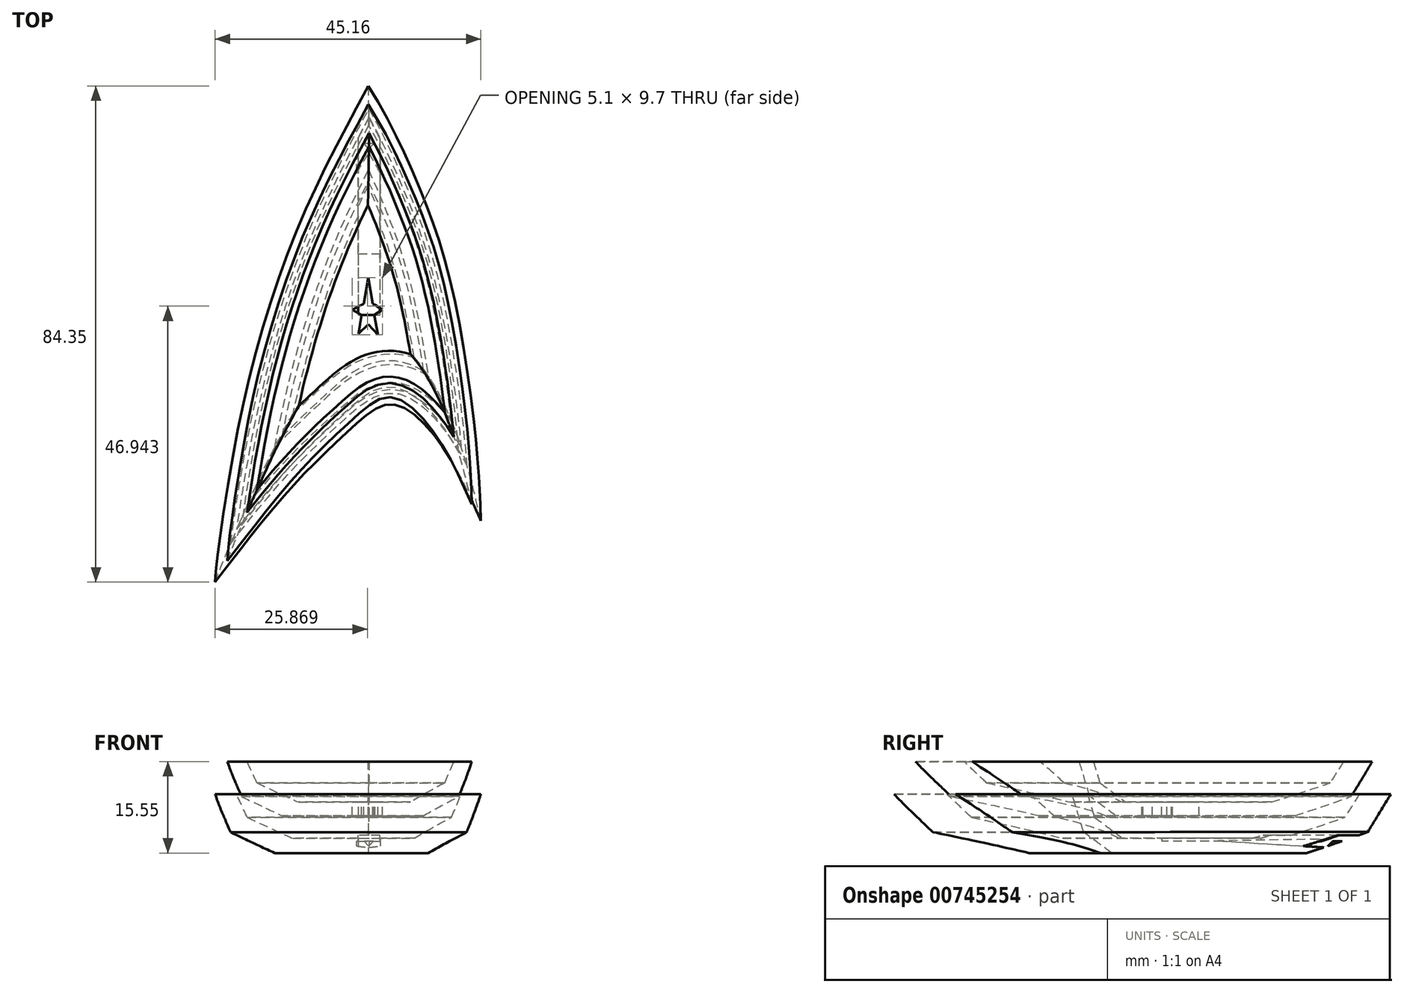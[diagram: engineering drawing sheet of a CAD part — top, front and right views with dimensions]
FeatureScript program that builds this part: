
annotation { "Feature Type Name" : "Feature", "Feature Type Description" : "" }
export const myFeature = defineFeature(function(context is Context, id is Id, definition is map)
    precondition{}
    {
        {
            var Q0;
            Q0=qCreatedBy(makeId("Top.planeOp"),FACE);
            var sketch = newSketch(context, id + "F0", { "sketchPlane" : qUnion([Q0])});
            skFitSpline(sketch, "E0", {"points": [v(0, 38.9) * mm, v(-11.48, 15.96) * mm, v(-21.55, -16.52) * mm, v(-25.85, -43.01) * mm, v(-26.03, -45.44) * mm], "startDerivative": vector(-41.53, -76.48) * mm, "endDerivative": vector(-0.94, -19.8) * mm});
            skFitSpline(sketch, "E1", {"points": [v(-26.03, -45.44) * mm, v(-12.6, -28.83) * mm, v(-2.7, -19.13) * mm, v(4.2, -15.2) * mm, v(12.4, -22.11) * mm, v(19.13, -34.99) * mm], "startDerivative": vector(53.97, 70.22) * mm, "endDerivative": vector(28.13, -63.45) * mm});
            skFitSpline(sketch, "E2", {"points": [v(0, 38.9) * mm, v(8.31, 22.5) * mm, v(14.28, 4.39) * mm, v(18.38, -22.3) * mm, v(19.13, -34.99) * mm], "startDerivative": vector(40.07, -63.37) * mm, "endDerivative": vector(1.63, -55.12) * mm});
            skSolve(sketch);
        }
        {
            var Q0;
            Q0=qCreatedBy(makeId("Top.planeOp"),FACE);
            cPlane(context, id + "F1", {"entities" : qUnion([Q0]), "cplaneType" : CPlaneType.OFFSET, "offset" : 25 * mm, "width" : 150 * mm, "height" : 150 * mm});
        }
        {
            var Q0;
            Q0=makeQuery(id+"F0.imprint","IMPRINT",FACE,{"disambiguationData":[TD([[makeQuery(id+"F0.imprint","IMPRINT",EDGE,{"derivedFrom":sQuery(id+"F0.wireOp",EDGE,"E0")}),1.0]])]});
            extrude(context, id + "F2", {"entities" : qUnion([Q0]), "depth" : 10 * mm, "offsetDistance" : 25 * mm});
        }
        {
            var Q0;
            Q0=makeQuery(id+"F2.opExtrude","CAP_EDGE",EDGE,{"disambiguationData":[OSD([sQuery(id+"F0.wireOp",EDGE,"E2")])],"isStart":true});
            var Q1;
            Q1=makeQuery(id+"F2.opExtrude","CAP_EDGE",EDGE,{"disambiguationData":[OSD([sQuery(id+"F0.wireOp",EDGE,"E1")])],"isStart":true});
            var Q2;
            Q2=makeQuery(id+"F2.opExtrude","CAP_EDGE",EDGE,{"disambiguationData":[OSD([sQuery(id+"F0.wireOp",EDGE,"E0")])],"isStart":true});
            chamfer(context, id + "F3", {"entities" : qUnion([Q0, Q1, Q2]), "chamferType" : ChamferType.TWO_OFFSETS, "width1" : 3 * mm, "oppositeDirection" : false, "width2" : 10 * mm, "tangentPropagation" : true});
        }
        {
            var Q0;
            Q0=makeQuery(id+"F2.opExtrude","CAP_FACE",FACE,{"disambiguationData":[OSD([sQuery(id+"F0.wireOp",EDGE,"E0"),sQuery(id+"F0.wireOp",EDGE,"E1"),sQuery(id+"F0.wireOp",EDGE,"E2")])],"isStart":false});
            shell(context, id + "F4", {"entities" : qUnion([Q0]), "thickness" : 2.5 * mm});
        }
        {
            var Q0;
            {var subQ0=sQuery(id+"F0.wireOp",EDGE,"E2");Q0=makeQuery(id+"F3.opChamfer","BLEND_EDGE",EDGE,{"blendedFrom":[makeQuery(id+"F2.opExtrude","CAP_EDGE",EDGE,{"disambiguationData":[OSD([subQ0])],"isStart":true}),makeQuery(id+"F2.opExtrude","CAP_FACE",FACE,{"disambiguationData":[OSD([sQuery(id+"F0.wireOp",EDGE,"E0"),sQuery(id+"F0.wireOp",EDGE,"E1"),subQ0])],"isStart":true})],"blendedInto":[makeQuery(id+"F2.opExtrude","CAP_FACE",FACE,{"disambiguationData":[OSD([sQuery(id+"F0.wireOp",EDGE,"E0"),sQuery(id+"F0.wireOp",EDGE,"E1"),subQ0])],"isStart":true})]});}
            var Q1;
            {var subQ0=sQuery(id+"F0.wireOp",EDGE,"E1");Q1=makeQuery(id+"F3.opChamfer","BLEND_EDGE",EDGE,{"blendedFrom":[makeQuery(id+"F2.opExtrude","CAP_EDGE",EDGE,{"disambiguationData":[OSD([subQ0])],"isStart":true}),makeQuery(id+"F2.opExtrude","CAP_FACE",FACE,{"disambiguationData":[OSD([sQuery(id+"F0.wireOp",EDGE,"E0"),subQ0,sQuery(id+"F0.wireOp",EDGE,"E2")])],"isStart":true})],"blendedInto":[makeQuery(id+"F2.opExtrude","CAP_FACE",FACE,{"disambiguationData":[OSD([sQuery(id+"F0.wireOp",EDGE,"E0"),subQ0,sQuery(id+"F0.wireOp",EDGE,"E2")])],"isStart":true})]});}
            var Q2;
            {var subQ0=sQuery(id+"F0.wireOp",EDGE,"E0");Q2=makeQuery(id+"F3.opChamfer","BLEND_EDGE",EDGE,{"blendedFrom":[makeQuery(id+"F2.opExtrude","CAP_EDGE",EDGE,{"disambiguationData":[OSD([subQ0])],"isStart":true}),makeQuery(id+"F2.opExtrude","CAP_FACE",FACE,{"disambiguationData":[OSD([subQ0,sQuery(id+"F0.wireOp",EDGE,"E1"),sQuery(id+"F0.wireOp",EDGE,"E2")])],"isStart":true})],"blendedInto":[makeQuery(id+"F2.opExtrude","CAP_FACE",FACE,{"disambiguationData":[OSD([subQ0,sQuery(id+"F0.wireOp",EDGE,"E1"),sQuery(id+"F0.wireOp",EDGE,"E2")])],"isStart":true})]});}
            chamfer(context, id + "F5", {"entities" : qUnion([Q0, Q1, Q2]), "width" : 5 * mm, "tangentPropagation" : true});
        }
        {
            var Q0;
            {var subQ0=sQuery(id+"F0.wireOp",EDGE,"E2");var subQ1=sQuery(id+"F0.wireOp",EDGE,"E1");var subQ2=sQuery(id+"F0.wireOp",EDGE,"E0");Q0=makeQuery(id+"F4.opShell","OFFSET_EDGE",EDGE,{"disambiguationData":[OSD([subQ2,subQ1,subQ0]),TDD([makeQuery(id+"F3.opChamfer","BLEND_EDGE",EDGE,{"blendedFrom":[makeQuery(id+"F2.opExtrude","CAP_EDGE",EDGE,{"disambiguationData":[OSD([subQ0])],"isStart":true}),makeQuery(id+"F2.opExtrude","CAP_FACE",FACE,{"disambiguationData":[OSD([subQ2,subQ1,subQ0])],"isStart":true})],"blendedInto":[makeQuery(id+"F2.opExtrude","CAP_FACE",FACE,{"disambiguationData":[OSD([subQ2,subQ1,subQ0])],"isStart":true})]})])]});}
            var Q1;
            {var subQ0=sQuery(id+"F0.wireOp",EDGE,"E2");var subQ1=sQuery(id+"F0.wireOp",EDGE,"E1");var subQ2=sQuery(id+"F0.wireOp",EDGE,"E0");Q1=makeQuery(id+"F4.opShell","OFFSET_EDGE",EDGE,{"disambiguationData":[OSD([subQ2,subQ1,subQ0]),TDD([makeQuery(id+"F3.opChamfer","BLEND_EDGE",EDGE,{"blendedFrom":[makeQuery(id+"F2.opExtrude","CAP_EDGE",EDGE,{"disambiguationData":[OSD([subQ2])],"isStart":true}),makeQuery(id+"F2.opExtrude","CAP_FACE",FACE,{"disambiguationData":[OSD([subQ2,subQ1,subQ0])],"isStart":true})],"blendedInto":[makeQuery(id+"F2.opExtrude","CAP_FACE",FACE,{"disambiguationData":[OSD([subQ2,subQ1,subQ0])],"isStart":true})]})])]});}
            var Q2;
            {var subQ0=sQuery(id+"F0.wireOp",EDGE,"E2");var subQ1=sQuery(id+"F0.wireOp",EDGE,"E1");var subQ2=sQuery(id+"F0.wireOp",EDGE,"E0");Q2=makeQuery(id+"F4.opShell","OFFSET_EDGE",EDGE,{"disambiguationData":[OSD([subQ2,subQ1,subQ0]),TDD([makeQuery(id+"F3.opChamfer","BLEND_EDGE",EDGE,{"blendedFrom":[makeQuery(id+"F2.opExtrude","CAP_EDGE",EDGE,{"disambiguationData":[OSD([subQ1])],"isStart":true}),makeQuery(id+"F2.opExtrude","CAP_FACE",FACE,{"disambiguationData":[OSD([subQ2,subQ1,subQ0])],"isStart":true})],"blendedInto":[makeQuery(id+"F2.opExtrude","CAP_FACE",FACE,{"disambiguationData":[OSD([subQ2,subQ1,subQ0])],"isStart":true})]})])]});}
            chamfer(context, id + "F6", {"entities" : qUnion([Q0, Q1, Q2]), "width" : 5 * mm, "tangentPropagation" : true});
        }
        {
            var Q0;
            Q0=makeQuery(id+"F2.opExtrude","SWEPT_BODY",BODY,{"disambiguationData":[OSD([sQuery(id+"F0.wireOp",EDGE,"E0"),sQuery(id+"F0.wireOp",EDGE,"E1"),sQuery(id+"F0.wireOp",EDGE,"E2")])]});
            transform(context, id + "F7", {"entities" : qUnion([Q0]), "transformType" : TransformType.TRANSLATION_3D, "dx" : 0 * mm, "dy" : 0 * mm, "dz" : 6.9 * mm, "makeCopy" : true});
        }
        {
            var Q0;
            Q0=makeQuery(id+"F7.opPattern","COPY",FACE,{"derivedFrom":makeQuery(id+"F4.opShell","OFFSET_FACE",FACE,{"disambiguationData":[OSD([sQuery(id+"F0.wireOp",EDGE,"E0"),sQuery(id+"F0.wireOp",EDGE,"E1"),sQuery(id+"F0.wireOp",EDGE,"E2")])]}),"instanceName":"1"});
            var sketch = newSketch(context, id + "F8", { "sketchPlane" : qUnion([Q0])});
            skLineSegment(sketch, "E3", {"start": v(0, 6.9) * mm, "end": v(-0.83, 2.03) * mm});
            skLineSegment(sketch, "E4", {"start": v(-0.83, 2.03) * mm, "end": v(-2.95, 0.97) * mm});
            skLineSegment(sketch, "E5", {"start": v(-2.95, 0.97) * mm, "end": v(-1.23, 0) * mm});
            skLineSegment(sketch, "E6", {"start": v(-1.23, 0) * mm, "end": v(-1.82, -3.45) * mm});
            skLineSegment(sketch, "E7", {"start": v(-1.82, -3.45) * mm, "end": v(0, -1.73) * mm});
            skLineSegment(sketch, "E8", {"start": v(0, -1.73) * mm, "end": v(1.8, -3.64) * mm});
            skLineSegment(sketch, "E9", {"start": v(1.8, -3.64) * mm, "end": v(1.08, 0) * mm});
            skLineSegment(sketch, "E10", {"start": v(1.08, 0) * mm, "end": v(2.6, 0.97) * mm});
            skLineSegment(sketch, "E11", {"start": v(2.6, 0.97) * mm, "end": v(1.21, 1.83) * mm});
            skLineSegment(sketch, "E12", {"start": v(1.21, 1.83) * mm, "end": v(0.85, 2.04) * mm});
            skLineSegment(sketch, "E13", {"start": v(0.85, 2.04) * mm, "end": v(0, 6.9) * mm});
            skSolve(sketch);
        }
        {
            var Q0;
            Q0=makeQuery(id+"F8.imprint","IMPRINT",FACE,{"disambiguationData":[TD([[makeQuery(id+"F8.imprint","IMPRINT",EDGE,{"derivedFrom":sQuery(id+"F8.wireOp",EDGE,"E3")}),1.0]])]});
            extrude(context, id + "F9", {"entities" : qUnion([Q0]), "operationType" : NewBodyOperationType.REMOVE, "oppositeDirection" : true, "depth" : 5 * mm, "offsetDistance" : 25 * mm});
        }
        {
            var Q0;
            Q0=makeQuery(id+"F7.opPattern","COPY",BODY,{"derivedFrom":makeQuery(id+"F2.opExtrude","SWEPT_BODY",BODY,{"disambiguationData":[OSD([sQuery(id+"F0.wireOp",EDGE,"E0"),sQuery(id+"F0.wireOp",EDGE,"E1"),sQuery(id+"F0.wireOp",EDGE,"E2")])]}),"instanceName":"1"});
            var Q1;
            Q1=qCreatedBy(makeId("Origin.pointOp"),VERTEX);
            var Q2;
            Q2=qCreatedBy(makeId("Origin.pointOp"),VERTEX);
            transform(context, id + "F10", {"entities" : qUnion([Q0]), "transformType" : TransformType.SCALE_UNIFORMLY, "scale" : 0.92, "scalePoint" : qUnion([Q2]), "makeCopy" : false});
        }
        {
            var Q0;
            Q0=qCreatedBy(makeId("Front.planeOp"),FACE);
            var sketch = newSketch(context, id + "F11", { "sketchPlane" : qUnion([Q0])});
            skLineSegment(sketch, "E14.bottom", {"start": v(-1.71, 3.03) * mm, "end": v(1.98, 3.03) * mm});
            skLineSegment(sketch, "E14.top", {"start": v(-1.71, 2.02) * mm, "end": v(1.98, 2.02) * mm});
            skLineSegment(sketch, "E14.left", {"start": v(-1.71, 3.03) * mm, "end": v(-1.71, 2.02) * mm});
            skLineSegment(sketch, "E14.right", {"start": v(1.98, 3.03) * mm, "end": v(1.98, 2.02) * mm});
            skSolve(sketch);
        }
        {
            var Q0;
            Q0=makeQuery(id+"F11.imprint","IMPRINT",FACE,{"disambiguationData":[TD([[makeQuery(id+"F11.imprint","IMPRINT",EDGE,{"derivedFrom":sQuery(id+"F11.wireOp",EDGE,"E14.bottom")}),-1.0]])]});
            extrude(context, id + "F12", {"entities" : qUnion([Q0]), "operationType" : NewBodyOperationType.REMOVE, "oppositeDirection" : true, "depth" : 50 * mm, "offsetDistance" : 25 * mm});
        }
        {
            var Q0;
            Q0=qCreatedBy(makeId("Right.planeOp"),FACE);
            var sketch = newSketch(context, id + "F13", { "sketchPlane" : qUnion([Q0])});
            skLineSegment(sketch, "E15", {"start": v(9.63, 2.07) * mm, "end": v(27.97, 0.93) * mm});
            skLineSegment(sketch, "E16", {"start": v(27.97, 0.93) * mm, "end": v(29.19, 2.1) * mm});
            skLineSegment(sketch, "E17", {"start": v(29.19, 2.1) * mm, "end": v(26.72, 2.35) * mm});
            skLineSegment(sketch, "E18", {"start": v(26.72, 2.35) * mm, "end": v(9.63, 2.07) * mm});
            skSolve(sketch);
        }
        {
            var Q0;
            Q0=makeQuery(id+"F13.imprint","IMPRINT",FACE,{"disambiguationData":[TD([[makeQuery(id+"F13.imprint","IMPRINT",EDGE,{"derivedFrom":sQuery(id+"F13.wireOp",EDGE,"E15")}),1.0]])]});
            extrude(context, id + "F14", {"entities" : qUnion([Q0]), "operationType" : NewBodyOperationType.REMOVE, "depth" : 2 * mm, "offsetDistance" : 25 * mm});
        }
        {
            var Q0;
            Q0=makeQuery(id+"F14.boolean.opBoolean","COPY",FACE,{"derivedFrom":makeQuery(id+"F14.opExtrude","CAP_FACE",FACE,{"disambiguationData":[OSD([sQuery(id+"F13.wireOp",EDGE,"E15"),sQuery(id+"F13.wireOp",EDGE,"E16"),sQuery(id+"F13.wireOp",EDGE,"E17"),sQuery(id+"F13.wireOp",EDGE,"E18")])],"isStart":true})});
            extrude(context, id + "F15", {"entities" : qUnion([Q0]), "operationType" : NewBodyOperationType.REMOVE, "oppositeDirection" : true, "depth" : 2 * mm, "offsetDistance" : 25 * mm});
        }
        {
            var Q0;
            Q0=makeQuery(id+"F15.boolean.opBoolean","COPY",FACE,{"derivedFrom":makeQuery(id+"F15.opExtrude","CAP_FACE",FACE,{"disambiguationData":[OSD([sQuery(id+"F13.wireOp",EDGE,"E15"),sQuery(id+"F13.wireOp",EDGE,"E16"),sQuery(id+"F13.wireOp",EDGE,"E17"),sQuery(id+"F13.wireOp",EDGE,"E18")])],"isStart":false})});
            extrude(context, id + "F16", {"entities" : qUnion([Q0]), "operationType" : NewBodyOperationType.ADD, "depth" : 0.29 * mm, "offsetDistance" : 25 * mm});
        }
    });
